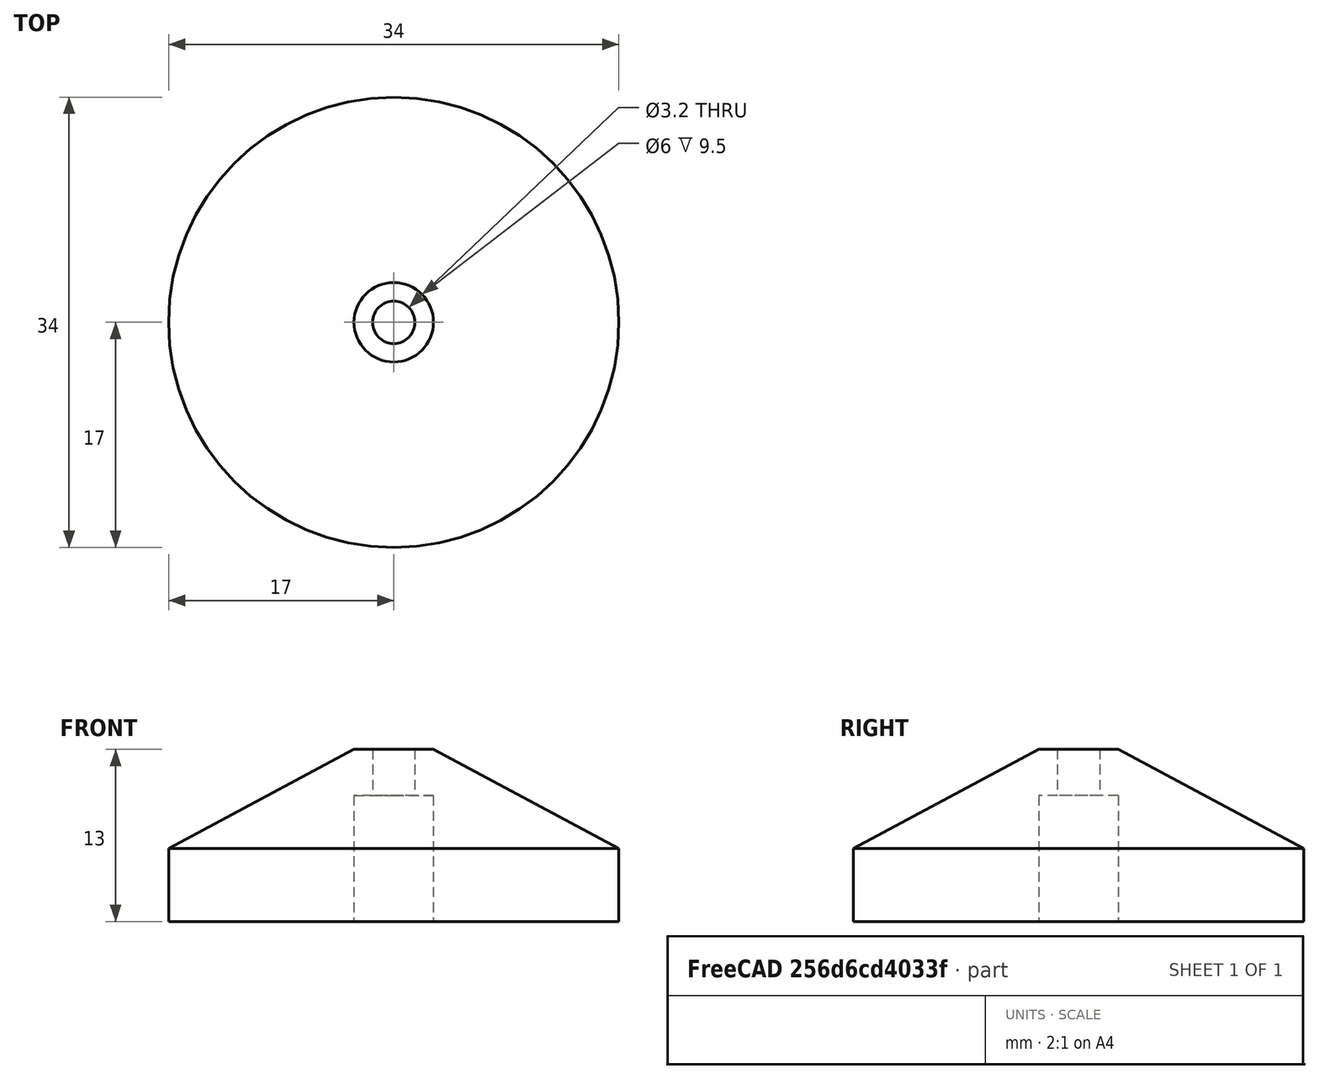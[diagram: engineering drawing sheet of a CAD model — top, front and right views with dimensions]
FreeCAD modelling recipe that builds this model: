
FCSTD DOCUMENT  (FreeCAD 0.21R33668 +26 (Git))
Label: BobbinSocket_R_A1
License: All rights reserved
LicenseURL: http://en.wikipedia.org/wiki/All_rights_reserved
objects: Sketcher::SketchObject×1, PartDesign::Revolution×1, PartDesign::Body×1, App::Part×1
note: 4 computed .brp shape members not serialized (recipe doc carries the construction recipe); baked Part::Feature solids carry a one-line shape summary decoded from their .brp

FEATURE [Sketcher::SketchObject] Sketch002
  FullyConstrained = true
  MapMode = 5
  Placement = pos=(0,0,0) rot=(0.57735,0.57735,0.57735;2.0944rad)
  Support = -> [YZ_Plane001]
  sketch-geometry (7):
    g0: LineSegment StartX=1.6 StartY=13 StartZ=0 EndX=1.6 EndY=9.5 EndZ=0
    g1: LineSegment StartX=17 StartY=0 StartZ=0 EndX=17 EndY=5.5 EndZ=0
    g2: LineSegment StartX=1.6 StartY=9.5 StartZ=0 EndX=3 EndY=9.5 EndZ=0
    g3: LineSegment StartX=3 StartY=9.5 StartZ=0 EndX=3 EndY=0 EndZ=0
    g4: LineSegment StartX=3 StartY=0 StartZ=0 EndX=17 EndY=0 EndZ=0
    g5: LineSegment StartX=1.6 StartY=13 StartZ=0 EndX=3 EndY=13 EndZ=0
    g6: LineSegment StartX=3 StartY=13 StartZ=0 EndX=17 EndY=5.5 EndZ=0
  constraints (21):
    c: PointOnObject(g1,g-1)
    c: Vertical(g1)
    c: DistanceX(g-1,g0) = 1.6
    c: Vertical(g0)
    c: Coincident(g0,g2)
    c: Coincident(g2,g3)
    c: PointOnObject(g3,g-1)
    c: Vertical(g3)
    c: Coincident(g3,g4)
    c: Coincident(g4,g1)
    c: DistanceX(g-1,g3) = 3
    c: DistanceY(g1,g1) = 5.5
    c: DistanceY(g-1,g0) = 13
    c: DistanceX(g-1,g1) = 17
    c: Horizontal(g2)
    c: DistanceY(g-1,g0) = 9.5
    c: Coincident(g0,g5)
    c: Horizontal(g5)
    c: Coincident(g5,g6)
    c: Coincident(g6,g1)
    c: DistanceX(g-1,g5) = 3
FEATURE [PartDesign::Revolution] Revolution
  AllowMultiFace = false
  Angle = 360
  Axis = (-2e-16,3e-16,1)
  Base = (0,0,0)
  Placement = pos=(0,0,0) rot=(1,1,1;2.0944rad)
  Profile = -> Sketch002
  ReferenceAxis = -> Sketch002 [V_Axis]
  Reversed = true
FEATURE [PartDesign::Body] RevolutionBody
  Group = -> [Sketch002,Revolution]
  Origin = -> Origin001
  Tip = -> Revolution
FEATURE [App::Part] Part
  Group = -> [RevolutionBody]
  Origin = -> Origin
